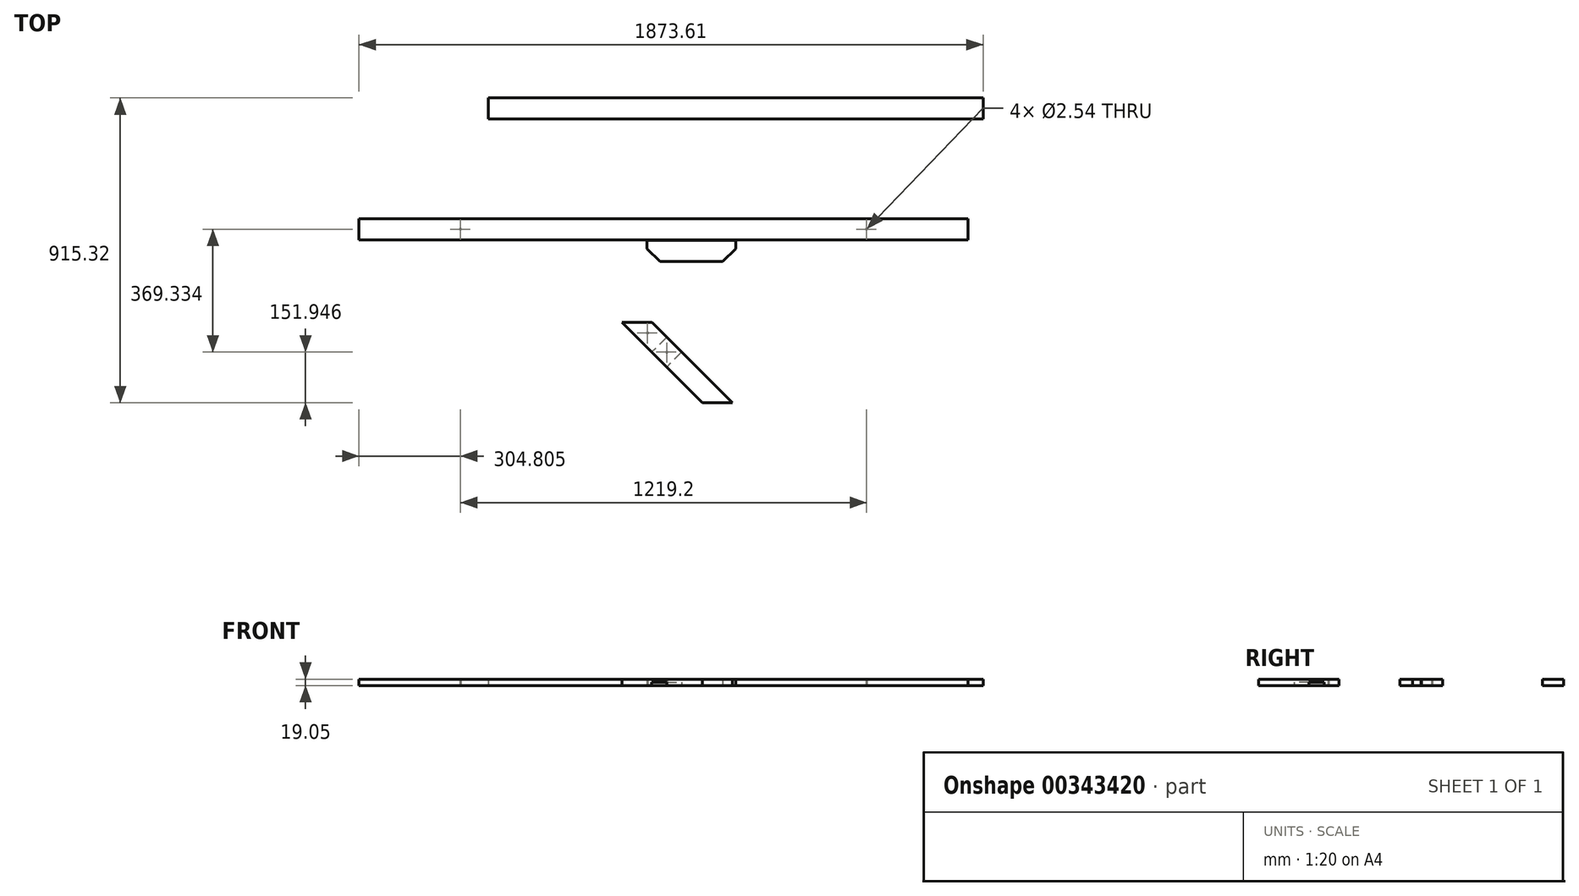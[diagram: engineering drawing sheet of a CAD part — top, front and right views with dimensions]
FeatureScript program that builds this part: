
annotation { "Feature Type Name" : "Feature", "Feature Type Description" : "" }
export const myFeature = defineFeature(function(context is Context, id is Id, definition is map)
    precondition{}
    {
        {
            var Q0;
            Q0=qCreatedBy(makeId("Top.planeOp"),FACE);
            var sketch = newSketch(context, id + "F0", { "sketchPlane" : qUnion([Q0])});
            skLineSegment(sketch, "E0", {"start": v(-1722.28, 311.18) * mm, "end": v(-1722.28, 247.68) * mm});
            skLineSegment(sketch, "E1", {"start": v(-1722.28, 247.68) * mm, "end": v(106.52, 247.68) * mm});
            skLineSegment(sketch, "E2", {"start": v(106.52, 247.68) * mm, "end": v(106.52, 311.18) * mm});
            skLineSegment(sketch, "E3", {"start": v(106.52, 311.18) * mm, "end": v(-1722.28, 311.18) * mm});
            skLineSegment(sketch, "E4", {"start": v(106.52, 279.43) * mm, "end": v(-198.28, 279.43) * mm});
            skLineSegment(sketch, "E5", {"start": v(106.52, 279.43) * mm, "end": v(-1417.48, 279.43) * mm});
            skCircle(sketch, "E6", {"center": v(-1417.48, 279.43) * mm, "radius": 1.27 * mm});
            skCircle(sketch, "E7", {"center": v(-198.28, 279.43) * mm, "radius": 1.27 * mm});
            skSolve(sketch);
        }
        {
            var Q0;
            Q0=qCreatedBy(makeId("Top.planeOp"),FACE);
            var sketch = newSketch(context, id + "F1", { "sketchPlane" : qUnion([Q0])});
            skLineSegment(sketch, "E8", {"start": v(-857.87, 245.6) * mm, "end": v(-857.87, 182.1) * mm});
            skLineSegment(sketch, "E9", {"start": v(-818.45, 182.1) * mm, "end": v(-630.58, 182.1) * mm});
            skLineSegment(sketch, "E10", {"start": v(-591.17, 220.2) * mm, "end": v(-591.17, 245.6) * mm});
            skLineSegment(sketch, "E11", {"start": v(-591.17, 245.6) * mm, "end": v(-857.87, 245.6) * mm});
            skLineSegment(sketch, "E12", {"start": v(-724.52, 89.83) * mm, "end": v(-724.52, 245.6) * mm});
            skPoint(sketch, "E12.endSnap0", {"position": v(-724.52, 245.6) * mm});
            skLineSegment(sketch, "E13", {"start": v(-591.17, 100.72) * mm, "end": v(-591.17, 245.6) * mm});
            skLineSegment(sketch, "E14", {"start": v(-591.17, 182.1) * mm, "end": v(-591.17, 220.2) * mm});
            skLineSegment(sketch, "E15", {"start": v(-630.58, 182.1) * mm, "end": v(-591.17, 220.2) * mm});
            skLineSegment(sketch, "E16.MirrorCS", {"start": v(-818.45, 182.1) * mm, "end": v(-857.87, 220.2) * mm});
            skSolve(sketch);
        }
        {
            var Q0;
            Q0=qCreatedBy(makeId("Top.planeOp"),FACE);
            var sketch = newSketch(context, id + "F2", { "sketchPlane" : qUnion([Q0])});
            skLineSegment(sketch, "E17", {"start": v(-932.56, -0.55) * mm, "end": v(-842.76, -0.55) * mm});
            skLineSegment(sketch, "E18", {"start": v(-798.3, -45) * mm, "end": v(-843.21, -89.9) * mm});
            skLineSegment(sketch, "E19.0", {"start": v(-753.4, -89.9) * mm, "end": v(-798.3, -134.8) * mm});
            skLineSegment(sketch, "E20.MirrorCS", {"start": v(-842.76, -0.55) * mm, "end": v(-601.46, -241.85) * mm});
            skLineSegment(sketch, "E21.MirrorCS", {"start": v(-932.56, -0.55) * mm, "end": v(-691.26, -241.85) * mm});
            skLineSegment(sketch, "E22.MirrorCS", {"start": v(-856.8, -31.4) * mm, "end": v(-855.01, -33.2) * mm});
            skCircle(sketch, "E23", {"center": v(-855.91, -32.3) * mm, "radius": 1.27 * mm});
            skCircle(sketch, "E24", {"center": v(-798.3, -89.9) * mm, "radius": 1.27 * mm});
            skLineSegment(sketch, "E25.trimOffspring", {"start": v(-691.26, -241.85) * mm, "end": v(-601.46, -241.85) * mm});
            skLineSegment(sketch, "E26.trimOffspring", {"start": v(-854.64, -32.3) * mm, "end": v(-857.18, -32.3) * mm});
            skPoint(sketch, "E27.orphan", {"position": v(-887.66, -0.55) * mm});
            skLineSegment(sketch, "E28.trimOffspring", {"start": v(-797.41, -89) * mm, "end": v(-799.2, -90.8) * mm});
            skLineSegment(sketch, "E29.trimOffspring", {"start": v(-842.76, -0.55) * mm, "end": v(-932.56, -0.55) * mm});
            skLineSegment(sketch, "E30.trimOffspring", {"start": v(-799.2, -89) * mm, "end": v(-797.41, -90.8) * mm});
            skPoint(sketch, "E31.orphan", {"position": v(-646.36, -241.85) * mm});
            skSolve(sketch);
        }
        {
            var Q0;
            Q0=makeQuery(id+"F0.imprint","IMPRINT",FACE,{"disambiguationData":[TD([[makeQuery(id+"F0.imprint","IMPRINT",EDGE,{"derivedFrom":sQuery(id+"F0.wireOp",EDGE,"E0")}),1.0]])]});
            extrude(context, id + "F3", {"entities" : qUnion([Q0]), "depth" : 19.05 * mm});
        }
        {
            var Q0;
            {var subQ3=sQuery(id+"F1.wireOp",EDGE,"E15");Q0=makeQuery(id+"F1.imprint","IMPRINT",FACE,{"disambiguationData":[TD([[makeQuery(id+"F1.imprint","IMPRINT",EDGE,{"derivedFrom":subQ3}),1.0]])]});}
            var Q1;
            {var subQ5=sQuery(id+"F1.wireOp",EDGE,"E16.MirrorCS");Q1=makeQuery(id+"F1.imprint","IMPRINT",FACE,{"disambiguationData":[TD([[makeQuery(id+"F1.imprint","IMPRINT",EDGE,{"derivedFrom":subQ5}),-1.0]])]});}
            extrude(context, id + "F4", {"entities" : qUnion([Q0, Q1]), "depth" : 19.05 * mm});
        }
        {
            var Q0;
            {var subQ1=sQuery(id+"F2.wireOp",EDGE,"E18");Q0=makeQuery(id+"F2.imprint","IMPRINT",FACE,{"disambiguationData":[TD([[makeQuery(id+"F2.imprint","IMPRINT",EDGE,{"derivedFrom":subQ1}),-1.0]])]});}
            var Q1;
            {var subQ0=sQuery(id+"F2.wireOp",EDGE,"E19.0");Q1=makeQuery(id+"F2.imprint","IMPRINT",FACE,{"disambiguationData":[TD([[makeQuery(id+"F2.imprint","IMPRINT",EDGE,{"derivedFrom":subQ0}),1.0]])]});}
            var Q2;
            {var subQ1=sQuery(id+"F2.wireOp",EDGE,"E18");Q2=makeQuery(id+"F2.imprint","IMPRINT",FACE,{"disambiguationData":[TD([[makeQuery(id+"F2.imprint","IMPRINT",EDGE,{"derivedFrom":subQ1}),1.0]])]});}
            extrude(context, id + "F5", {"entities" : qUnion([Q0, Q1, Q2]), "depth" : 19.05 * mm});
        }
        {
            var Q0;
            {var subQ1=sQuery(id+"F2.wireOp",EDGE,"E18");Q0=makeQuery(id+"F2.imprint","IMPRINT",FACE,{"disambiguationData":[TD([[makeQuery(id+"F2.imprint","IMPRINT",EDGE,{"derivedFrom":subQ1}),1.0]])]});}
            extrude(context, id + "F6", {"entities" : qUnion([Q0]), "operationType" : NewBodyOperationType.REMOVE, "oppositeDirection" : true, "depth" : -9.52 * mm});
        }
        {
            var Q0;
            Q0=qCreatedBy(makeId("Top.planeOp"),FACE);
            var sketch = newSketch(context, id + "F7", { "sketchPlane" : qUnion([Q0])});
            skLineSegment(sketch, "E32", {"start": v(-1334.57, 673.47) * mm, "end": v(-1334.57, 609.97) * mm});
            skLineSegment(sketch, "E33", {"start": v(-1334.57, 609.97) * mm, "end": v(151.33, 609.97) * mm});
            skLineSegment(sketch, "E34", {"start": v(151.33, 609.97) * mm, "end": v(151.33, 673.47) * mm});
            skLineSegment(sketch, "E35", {"start": v(151.33, 673.47) * mm, "end": v(-1334.57, 673.47) * mm});
            skSolve(sketch);
        }
        {
            var Q0;
            Q0 = qSketchRegion(id + "F7", true);
            extrude(context, id + "F8", {"entities" : qUnion([Q0]), "depth" : 19.05 * mm});
        }
    });
